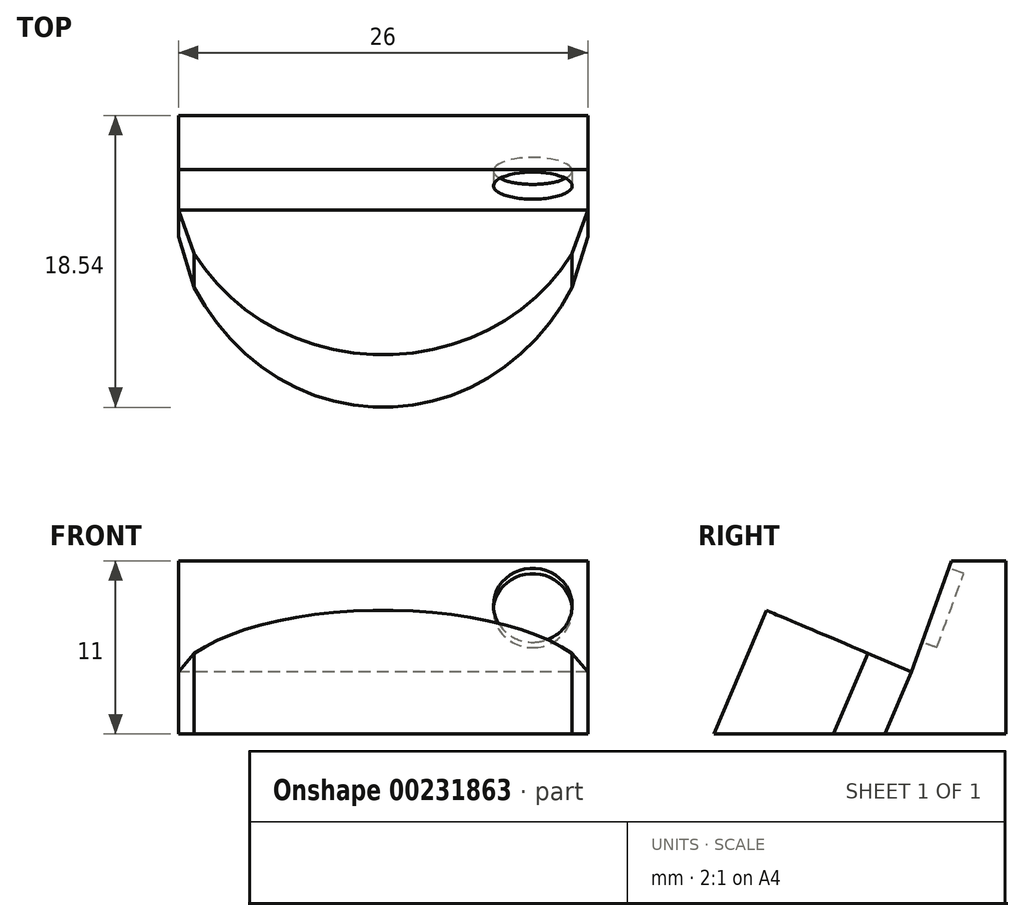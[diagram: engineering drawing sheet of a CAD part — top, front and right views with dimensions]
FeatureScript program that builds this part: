
annotation { "Feature Type Name" : "Feature", "Feature Type Description" : "" }
export const myFeature = defineFeature(function(context is Context, id is Id, definition is map)
    precondition{}
    {
        {
            var Q0;
            Q0=qCreatedBy(makeId("Right.planeOp"),FACE);
            var sketch = newSketch(context, id + "F0", { "sketchPlane" : qUnion([Q0])});
            skLineSegment(sketch, "E0", {"start": v(0, 11) * mm, "end": v(0, 0) * mm});
            skLineSegment(sketch, "E1.MirrorCS", {"start": v(0, 11) * mm, "end": v(-3.43, 11) * mm});
            skLineSegment(sketch, "E2.MirrorCS", {"start": v(-6, 3.95) * mm, "end": v(-3.43, 11) * mm});
            skLineSegment(sketch, "E3.MirrorCS", {"start": v(-20, 9.9) * mm, "end": v(-6, 3.95) * mm});
            skLineSegment(sketch, "E4.MirrorCS", {"start": v(-20, 0) * mm, "end": v(-20, 9.9) * mm});
            skLineSegment(sketch, "E5.MirrorCS", {"start": v(0, 0) * mm, "end": v(-20, 0) * mm});
            skSolve(sketch);
        }
        {
            var Q0;
            Q0=qSketchRegion(id+"F0",true);
            extrude(context, id + "F1", {"entities" : qUnion([Q0]), "depth" : 26 * mm});
        }
        {
            var Q0;
            Q0=makeQuery(id+"F1.opExtrude","SWEPT_FACE",FACE,{"disambiguationData":[OSD([sQuery(id+"F0.wireOp",EDGE,"E2.MirrorCS")])]});
            var sketch = newSketch(context, id + "F2", { "sketchPlane" : qUnion([Q0])});
            skCircle(sketch, "E6", {"center": v(22.5, 6.16) * mm, "radius": 2.5 * mm});
            skSolve(sketch);
        }
        {
            var Q0;
            Q0=qSketchRegion(id+"F2",true);
            extrude(context, id + "F3", {"entities" : qUnion([Q0]), "operationType" : NewBodyOperationType.REMOVE, "oppositeDirection" : true, "depth" : 1 * mm});
        }
        {
            var Q0;
            Q0=makeQuery(id+"F1.opExtrude","SWEPT_FACE",FACE,{"disambiguationData":[OSD([sQuery(id+"F0.wireOp",EDGE,"E3.MirrorCS")])]});
            var sketch = newSketch(context, id + "F4", { "sketchPlane" : qUnion([Q0])});
            skLineSegment(sketch, "E7", {"start": v(0, -10.07) * mm, "end": v(26, -10.07) * mm, "construction": true});
            skLineSegment(sketch, "E8", {"start": v(25, -10.07) * mm, "end": v(26, -7.07) * mm});
            skLineSegment(sketch, "E9", {"start": v(0, -7.07) * mm, "end": v(1, -10.07) * mm});
            skArc(sketch, "E10", {"start": v(1, -10.07) * mm, "mid": v(13, -17.07) * mm, "end": v(25, -10.07) * mm});
            skLineSegment(sketch, "E11", {"start": v(26, -7.07) * mm, "end": v(0, -7.07) * mm});
            skSolve(sketch);
        }
        {
            var Q0;
            {var subQ0=sQuery(id+"F4.wireOp",EDGE,"E9");Q0=makeQuery(id+"F4.imprint","IMPRINT",FACE,{"disambiguationData":[TD([[makeQuery(id+"F4.imprint","IMPRINT",EDGE,{"derivedFrom":subQ0}),-1.0]])]});}
            var Q1;
            {var subQ0=sQuery(id+"F4.wireOp",EDGE,"E8");Q1=makeQuery(id+"F4.imprint","IMPRINT",FACE,{"disambiguationData":[TD([[makeQuery(id+"F4.imprint","IMPRINT",EDGE,{"derivedFrom":subQ0}),-1.0]])]});}
            extrude(context, id + "F5", {"entities" : qUnion([Q0, Q1]), "operationType" : NewBodyOperationType.REMOVE, "endBound" : BoundingType.UP_TO_NEXT, "oppositeDirection" : true, "depth" : 25 * mm});
        }
    });
